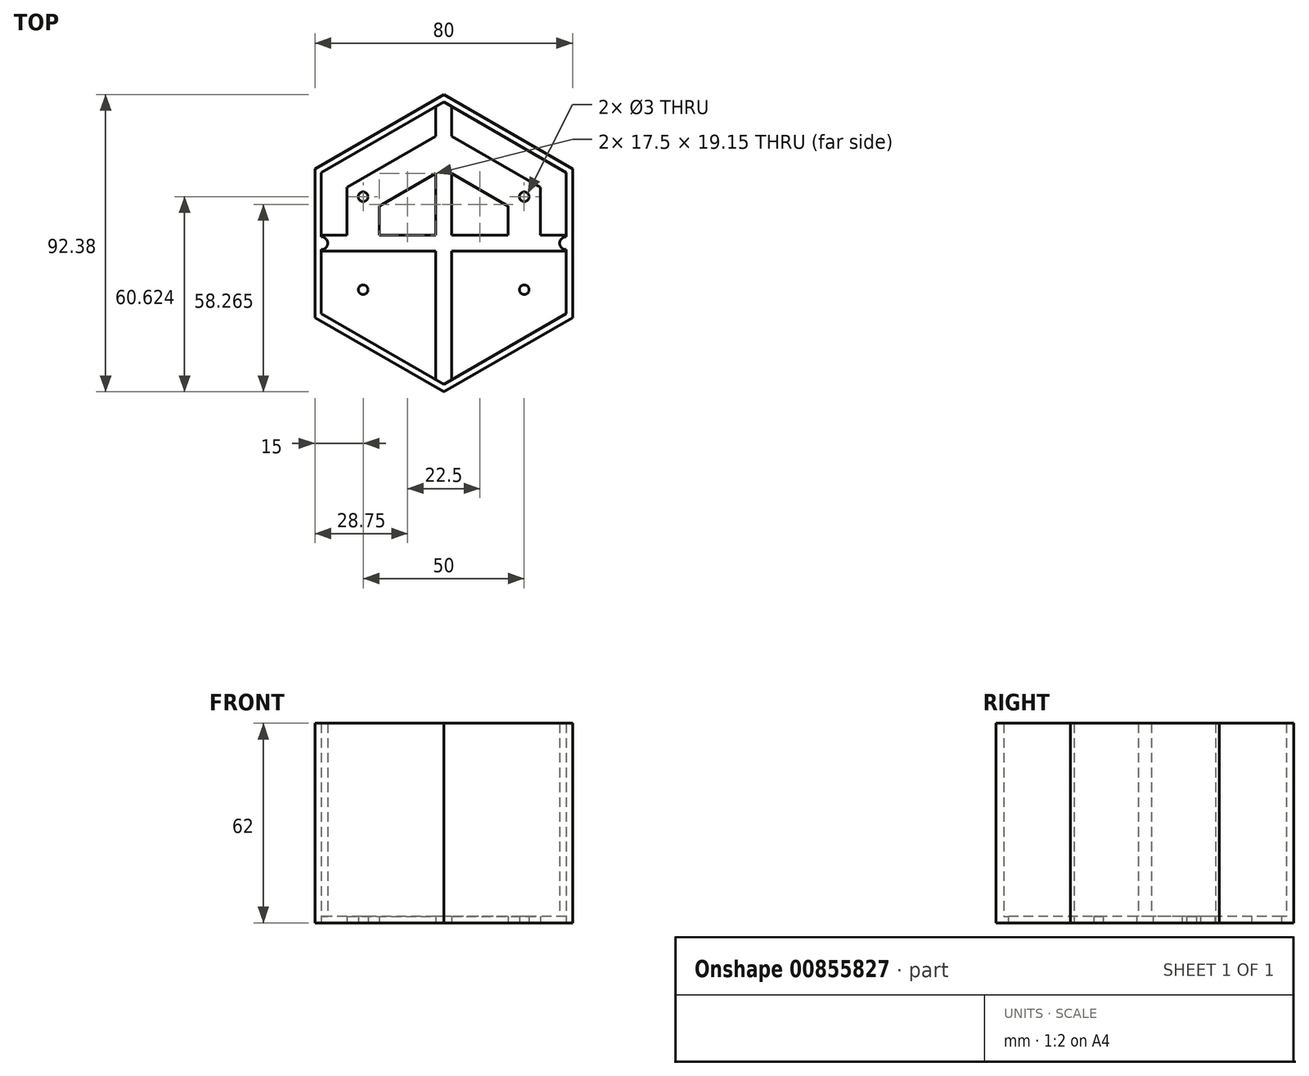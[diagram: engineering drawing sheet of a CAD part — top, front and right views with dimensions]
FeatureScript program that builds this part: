
annotation { "Feature Type Name" : "Feature", "Feature Type Description" : "" }
export const myFeature = defineFeature(function(context is Context, id is Id, definition is map)
    precondition{}
    {
        {
            var Q0;
            Q0=qCreatedBy(makeId("Top.planeOp"),FACE);
            var sketch = newSketch(context, id + "F0", { "sketchPlane" : qUnion([Q0])});
            skCircle(sketch, "E0.cCircle", {"center": v(0, 0) * mm, "radius": 40 * mm, "construction": true});
            skLineSegment(sketch, "E0.0", {"start": v(40, 23.1) * mm, "end": v(40, -23.1) * mm});
            skLineSegment(sketch, "E0.1", {"start": v(40, -23.1) * mm, "end": v(0, -46.19) * mm});
            skLineSegment(sketch, "E0.2", {"start": v(0, -46.19) * mm, "end": v(-40, -23.1) * mm});
            skLineSegment(sketch, "E0.3", {"start": v(-40, -23.1) * mm, "end": v(-40, 23.1) * mm});
            skLineSegment(sketch, "E0.4", {"start": v(-40, 23.1) * mm, "end": v(0, 46.19) * mm});
            skLineSegment(sketch, "E0.5", {"start": v(0, 46.19) * mm, "end": v(40, 23.1) * mm});
            skPoint(sketch, "E0.0.midPoint", {"position": v(40, 0) * mm});
            skCircle(sketch, "E1.cCircle", {"center": v(0, 0) * mm, "radius": 38 * mm, "construction": true});
            skLineSegment(sketch, "E1.0", {"start": v(38, 21.94) * mm, "end": v(38, -21.94) * mm});
            skLineSegment(sketch, "E1.1", {"start": v(38, -21.94) * mm, "end": v(0, -43.88) * mm});
            skLineSegment(sketch, "E1.2", {"start": v(0, -43.88) * mm, "end": v(-38, -21.94) * mm});
            skLineSegment(sketch, "E1.3", {"start": v(-38, -21.94) * mm, "end": v(-38, 21.94) * mm});
            skLineSegment(sketch, "E1.4", {"start": v(-38, 21.94) * mm, "end": v(0, 43.88) * mm});
            skLineSegment(sketch, "E1.5", {"start": v(0, 43.88) * mm, "end": v(38, 21.94) * mm});
            skPoint(sketch, "E1.0.midPoint", {"position": v(38, 0) * mm});
            skCircle(sketch, "E2.cCircle", {"center": v(0, 0) * mm, "radius": 30 * mm, "construction": true});
            skLineSegment(sketch, "E2.0", {"start": v(30, 17.32) * mm, "end": v(30, -17.32) * mm});
            skLineSegment(sketch, "E2.1", {"start": v(30, -17.32) * mm, "end": v(0, -34.64) * mm});
            skLineSegment(sketch, "E2.2", {"start": v(0, -34.64) * mm, "end": v(-30, -17.32) * mm});
            skLineSegment(sketch, "E2.3", {"start": v(-30, -17.32) * mm, "end": v(-30, 17.32) * mm});
            skLineSegment(sketch, "E2.4", {"start": v(-30, 17.32) * mm, "end": v(0, 34.64) * mm});
            skLineSegment(sketch, "E2.5", {"start": v(0, 34.64) * mm, "end": v(30, 17.32) * mm});
            skPoint(sketch, "E2.0.midPoint", {"position": v(30, 0) * mm});
            skCircle(sketch, "E3.cCircle", {"center": v(0, 0) * mm, "radius": 20 * mm, "construction": true});
            skLineSegment(sketch, "E3.0", {"start": v(20, 11.55) * mm, "end": v(20, -11.55) * mm});
            skLineSegment(sketch, "E3.1", {"start": v(20, -11.55) * mm, "end": v(0, -23.1) * mm});
            skLineSegment(sketch, "E3.2", {"start": v(0, -23.1) * mm, "end": v(-20, -11.55) * mm});
            skLineSegment(sketch, "E3.3", {"start": v(-20, -11.55) * mm, "end": v(-20, 11.55) * mm});
            skLineSegment(sketch, "E3.4", {"start": v(-20, 11.55) * mm, "end": v(0, 23.1) * mm});
            skLineSegment(sketch, "E3.5", {"start": v(0, 23.1) * mm, "end": v(20, 11.55) * mm});
            skPoint(sketch, "E3.0.midPoint", {"position": v(20, 0) * mm});
            skLineSegment(sketch, "E4.bottom", {"start": v(38, -2.5) * mm, "end": v(-38, -2.5) * mm});
            skLineSegment(sketch, "E4.top", {"start": v(38, 2.5) * mm, "end": v(-38, 2.5) * mm});
            skLineSegment(sketch, "E4.left", {"start": v(38, -2.5) * mm, "end": v(38, 2.5) * mm});
            skLineSegment(sketch, "E4.right", {"start": v(-38, -2.5) * mm, "end": v(-38, 2.5) * mm});
            skLineSegment(sketch, "E5.bottom", {"start": v(2.5, 44.74) * mm, "end": v(-2.5, 44.74) * mm});
            skLineSegment(sketch, "E5.top", {"start": v(2.5, -44.74) * mm, "end": v(-2.5, -44.74) * mm});
            skLineSegment(sketch, "E5.left", {"start": v(2.5, 44.74) * mm, "end": v(2.5, -44.74) * mm});
            skLineSegment(sketch, "E5.right", {"start": v(-2.5, 44.74) * mm, "end": v(-2.5, -44.74) * mm});
            skLineSegment(sketch, "E6", {"start": v(-30, 17.32) * mm, "end": v(-20, 11.55) * mm, "construction": true});
            skCircle(sketch, "E7", {"center": v(-25, 14.43) * mm, "radius": 1.5 * mm});
            skLineSegment(sketch, "E8", {"start": v(20, 11.55) * mm, "end": v(30, 17.32) * mm, "construction": true});
            skCircle(sketch, "E9", {"center": v(25, 14.43) * mm, "radius": 1.5 * mm});
            skLineSegment(sketch, "E10", {"start": v(-40, 0) * mm, "end": v(58.27, 0) * mm, "construction": true});
            skCircle(sketch, "E11.MirrorC", {"center": v(-25, -14.43) * mm, "radius": 1.5 * mm});
            skCircle(sketch, "E12.MirrorC", {"center": v(25, -14.43) * mm, "radius": 1.5 * mm});
            skArc(sketch, "E13", {"start": v(38, 2) * mm, "mid": v(36, 0) * mm, "end": v(38, -2) * mm});
            skArc(sketch, "E14", {"start": v(-38, -2) * mm, "mid": v(-36, 0) * mm, "end": v(-38, 2) * mm});
            skSolve(sketch);
        }
        {
            var Q0;
            {var subQ12=sQuery(id+"F0.wireOp",EDGE,"E5.bottom");var subQ18=sQuery(id+"F0.wireOp",EDGE,"E5.top");var subQ23=sQuery(id+"F0.wireOp",EDGE,"E0.3");var subQ40=sQuery(id+"F0.wireOp",EDGE,"E0.0");var subQ45=makeQuery(id+"F0.imprint","IMPRINT",EDGE,{"derivedFrom":subQ12});var subQ47=makeQuery(id+"F0.imprint","IMPRINT",EDGE,{"derivedFrom":subQ18});Q0=qUnion([makeQuery(id+"F0.imprint","IMPRINT",FACE,{"disambiguationData":[TD([[subQ47,1.0]])]}),makeQuery(id+"F0.imprint","IMPRINT",FACE,{"disambiguationData":[TD([[subQ45,-1.0]])]}),makeQuery(id+"F0.imprint","IMPRINT",FACE,{"disambiguationData":[TD([[subQ47,-1.0]])]}),makeQuery(id+"F0.imprint","IMPRINT",FACE,{"disambiguationData":[TD([[subQ45,1.0]])]}),makeQuery(id+"F0.imprint","IMPRINT",FACE,{"disambiguationData":[TD([[makeQuery(id+"F0.imprint","IMPRINT",EDGE,{"derivedFrom":subQ40}),-1.0]])]}),makeQuery(id+"F0.imprint","IMPRINT",FACE,{"disambiguationData":[TD([[makeQuery(id+"F0.imprint","IMPRINT",EDGE,{"derivedFrom":subQ23}),-1.0]])]})]);}
            var Q1;
            Q1=makeQuery(id+"F0.imprint","IMPRINT",FACE,{"disambiguationData":[TD([[makeQuery(id+"F0.imprint","IMPRINT",EDGE,{"derivedFrom":sQuery(id+"F0.wireOp",EDGE,"E7")}),-1.0]])]});
            var Q2;
            Q2=makeQuery(id+"F0.imprint","IMPRINT",FACE,{"disambiguationData":[TD([[makeQuery(id+"F0.imprint","IMPRINT",EDGE,{"derivedFrom":sQuery(id+"F0.wireOp",EDGE,"E9")}),-1.0]])]});
            var Q3;
            {var subQ7=sQuery(id+"F0.wireOp",EDGE,"E2.5");var subQ8=sQuery(id+"F0.wireOp",EDGE,"E2.4");var subQ9=makeQuery(id+"F0.imprint","INTERSECT",VERTEX,{"derivedFrom":[subQ8,subQ7]});Q3=makeQuery(id+"F0.imprint","IMPRINT",FACE,{"disambiguationData":[TD([[makeQuery(id+"F0.imprint","IMPRINT",EDGE,{"disambiguationData":[TD([[subQ9,1.0]])],"derivedFrom":subQ8}),-1.0]])]});}
            var Q4;
            {var subQ6=sQuery(id+"F0.wireOp",EDGE,"E1.4");var subQ9=sQuery(id+"F0.wireOp",EDGE,"E1.5");var subQ10=makeQuery(id+"F0.imprint","INTERSECT",VERTEX,{"derivedFrom":[subQ6,subQ9]});Q4=makeQuery(id+"F0.imprint","IMPRINT",FACE,{"disambiguationData":[TD([[makeQuery(id+"F0.imprint","IMPRINT",EDGE,{"disambiguationData":[TD([[subQ10,1.0]])],"derivedFrom":subQ6}),-1.0]])]});}
            var Q5;
            Q5=makeQuery(id+"F0.imprint","IMPRINT",FACE,{"disambiguationData":[TD([[makeQuery(id+"F0.imprint","IMPRINT",EDGE,{"derivedFrom":sQuery(id+"F0.wireOp",EDGE,"E11.MirrorC")}),1.0]])]});
            var Q6;
            {var subQ7=sQuery(id+"F0.wireOp",EDGE,"E2.2");var subQ8=sQuery(id+"F0.wireOp",EDGE,"E2.1");var subQ9=makeQuery(id+"F0.imprint","INTERSECT",VERTEX,{"derivedFrom":[subQ8,subQ7]});Q6=makeQuery(id+"F0.imprint","IMPRINT",FACE,{"disambiguationData":[TD([[makeQuery(id+"F0.imprint","IMPRINT",EDGE,{"disambiguationData":[TD([[subQ9,1.0]])],"derivedFrom":subQ8}),-1.0]])]});}
            var Q7;
            Q7=makeQuery(id+"F0.imprint","IMPRINT",FACE,{"disambiguationData":[TD([[makeQuery(id+"F0.imprint","IMPRINT",EDGE,{"derivedFrom":sQuery(id+"F0.wireOp",EDGE,"E12.MirrorC")}),1.0]])]});
            var Q8;
            {var subQ0=sQuery(id+"F0.wireOp",EDGE,"E4.bottom");var subQ1=sQuery(id+"F0.wireOp",EDGE,"E2.0");var subQ2=makeQuery(id+"F0.imprint","INTERSECT",VERTEX,{"derivedFrom":[subQ1,subQ0]});Q8=makeQuery(id+"F0.imprint","IMPRINT",FACE,{"disambiguationData":[TD([[makeQuery(id+"F0.imprint","IMPRINT",EDGE,{"disambiguationData":[TD([[subQ2,1.0]])],"derivedFrom":subQ1}),-1.0]])]});}
            var Q9;
            {var subQ5=sQuery(id+"F0.wireOp",EDGE,"E13");Q9=makeQuery(id+"F0.imprint","IMPRINT",FACE,{"disambiguationData":[TD([[makeQuery(id+"F0.imprint","IMPRINT",EDGE,{"derivedFrom":subQ5}),-1.0]])]});}
            var Q10;
            {var subQ0=sQuery(id+"F0.wireOp",EDGE,"E4.bottom");var subQ1=sQuery(id+"F0.wireOp",EDGE,"E3.0");var subQ2=makeQuery(id+"F0.imprint","INTERSECT",VERTEX,{"derivedFrom":[subQ1,subQ0]});Q10=makeQuery(id+"F0.imprint","IMPRINT",FACE,{"disambiguationData":[TD([[makeQuery(id+"F0.imprint","IMPRINT",EDGE,{"disambiguationData":[TD([[subQ2,1.0]])],"derivedFrom":subQ1}),-1.0]])]});}
            var Q11;
            {var subQ1=sQuery(id+"F0.wireOp",EDGE,"E3.5");var subQ7=sQuery(id+"F0.wireOp",EDGE,"E3.4");var subQ8=makeQuery(id+"F0.imprint","INTERSECT",VERTEX,{"derivedFrom":[subQ7,subQ1]});Q11=makeQuery(id+"F0.imprint","IMPRINT",FACE,{"disambiguationData":[TD([[makeQuery(id+"F0.imprint","IMPRINT",EDGE,{"disambiguationData":[TD([[subQ8,1.0]])],"derivedFrom":subQ7}),-1.0]])]});}
            var Q12;
            {var subQ0=sQuery(id+"F0.wireOp",EDGE,"E4.top");var subQ1=sQuery(id+"F0.wireOp",EDGE,"E3.3");var subQ2=makeQuery(id+"F0.imprint","INTERSECT",VERTEX,{"derivedFrom":[subQ1,subQ0]});Q12=makeQuery(id+"F0.imprint","IMPRINT",FACE,{"disambiguationData":[TD([[makeQuery(id+"F0.imprint","IMPRINT",EDGE,{"disambiguationData":[TD([[subQ2,1.0]])],"derivedFrom":subQ1}),-1.0]])]});}
            var Q13;
            {var subQ0=sQuery(id+"F0.wireOp",EDGE,"E4.top");var subQ1=sQuery(id+"F0.wireOp",EDGE,"E2.3");var subQ2=makeQuery(id+"F0.imprint","INTERSECT",VERTEX,{"derivedFrom":[subQ1,subQ0]});Q13=makeQuery(id+"F0.imprint","IMPRINT",FACE,{"disambiguationData":[TD([[makeQuery(id+"F0.imprint","IMPRINT",EDGE,{"disambiguationData":[TD([[subQ2,1.0]])],"derivedFrom":subQ1}),-1.0]])]});}
            var Q14;
            {var subQ5=sQuery(id+"F0.wireOp",EDGE,"E14");Q14=makeQuery(id+"F0.imprint","IMPRINT",FACE,{"disambiguationData":[TD([[makeQuery(id+"F0.imprint","IMPRINT",EDGE,{"derivedFrom":subQ5}),-1.0]])]});}
            var Q15;
            {var subQ5=sQuery(id+"F0.wireOp",EDGE,"E3.1");var subQ7=sQuery(id+"F0.wireOp",EDGE,"E3.2");var subQ8=makeQuery(id+"F0.imprint","INTERSECT",VERTEX,{"derivedFrom":[subQ5,subQ7]});Q15=makeQuery(id+"F0.imprint","IMPRINT",FACE,{"disambiguationData":[TD([[makeQuery(id+"F0.imprint","IMPRINT",EDGE,{"disambiguationData":[TD([[subQ8,1.0]])],"derivedFrom":subQ5}),-1.0]])]});}
            var Q16;
            {var subQ0=sQuery(id+"F0.wireOp",EDGE,"E5.right");var subQ1=sQuery(id+"F0.wireOp",EDGE,"E4.bottom");var subQ2=makeQuery(id+"F0.imprint","INTERSECT",VERTEX,{"derivedFrom":[subQ1,subQ0]});Q16=makeQuery(id+"F0.imprint","IMPRINT",FACE,{"disambiguationData":[TD([[makeQuery(id+"F0.imprint","IMPRINT",EDGE,{"disambiguationData":[TD([[subQ2,1.0]])],"derivedFrom":subQ1}),-1.0]])]});}
            var Q17;
            {var subQ7=sQuery(id+"F0.wireOp",EDGE,"E1.2");var subQ8=sQuery(id+"F0.wireOp",EDGE,"E1.1");var subQ9=makeQuery(id+"F0.imprint","INTERSECT",VERTEX,{"derivedFrom":[subQ8,subQ7]});Q17=makeQuery(id+"F0.imprint","IMPRINT",FACE,{"disambiguationData":[TD([[makeQuery(id+"F0.imprint","IMPRINT",EDGE,{"disambiguationData":[TD([[subQ9,1.0]])],"derivedFrom":subQ8}),-1.0]])]});}
            var Q18;
            {var subQ0=sQuery(id+"F0.wireOp",EDGE,"E14");Q18=makeQuery(id+"F0.imprint","IMPRINT",FACE,{"disambiguationData":[TD([[makeQuery(id+"F0.imprint","IMPRINT",EDGE,{"derivedFrom":subQ0}),1.0]])]});}
            var Q19;
            {var subQ0=sQuery(id+"F0.wireOp",EDGE,"E13");Q19=makeQuery(id+"F0.imprint","IMPRINT",FACE,{"disambiguationData":[TD([[makeQuery(id+"F0.imprint","IMPRINT",EDGE,{"derivedFrom":subQ0}),1.0]])]});}
            extrude(context, id + "F1", {"entities" : qUnion([Q0, Q1, Q2, Q3, Q4, Q5, Q6, Q7, Q8, Q9, Q10, Q11, Q12, Q13, Q14, Q15, Q16, Q17, Q18, Q19]), "depth" : 2 * mm, "offsetDistance" : 25 * mm});
        }
        {
            var Q0;
            Q0=makeQuery(id+"F1.opExtrude","CAP_FACE",FACE,{"disambiguationData":[OSD([sQuery(id+"F0.wireOp",EDGE,"E0.0"),sQuery(id+"F0.wireOp",EDGE,"E0.1"),sQuery(id+"F0.wireOp",EDGE,"E0.2"),sQuery(id+"F0.wireOp",EDGE,"E0.3"),sQuery(id+"F0.wireOp",EDGE,"E0.4"),sQuery(id+"F0.wireOp",EDGE,"E0.5"),sQuery(id+"F0.wireOp",EDGE,"E1.0"),sQuery(id+"F0.wireOp",EDGE,"E1.1"),sQuery(id+"F0.wireOp",EDGE,"E1.2"),sQuery(id+"F0.wireOp",EDGE,"E1.3"),sQuery(id+"F0.wireOp",EDGE,"E1.4"),sQuery(id+"F0.wireOp",EDGE,"E1.5"),sQuery(id+"F0.wireOp",EDGE,"E2.0"),sQuery(id+"F0.wireOp",EDGE,"E2.1"),sQuery(id+"F0.wireOp",EDGE,"E2.2"),sQuery(id+"F0.wireOp",EDGE,"E2.3"),sQuery(id+"F0.wireOp",EDGE,"E2.4"),sQuery(id+"F0.wireOp",EDGE,"E2.5"),sQuery(id+"F0.wireOp",EDGE,"E3.0"),sQuery(id+"F0.wireOp",EDGE,"E3.1"),sQuery(id+"F0.wireOp",EDGE,"E3.2"),sQuery(id+"F0.wireOp",EDGE,"E3.3"),sQuery(id+"F0.wireOp",EDGE,"E3.4"),sQuery(id+"F0.wireOp",EDGE,"E3.5"),sQuery(id+"F0.wireOp",EDGE,"E4.bottom"),sQuery(id+"F0.wireOp",EDGE,"E4.top"),sQuery(id+"F0.wireOp",EDGE,"E5.left"),sQuery(id+"F0.wireOp",EDGE,"E5.right"),sQuery(id+"F0.wireOp",EDGE,"E7"),sQuery(id+"F0.wireOp",EDGE,"E9"),sQuery(id+"F0.wireOp",EDGE,"E11.MirrorC"),sQuery(id+"F0.wireOp",EDGE,"E12.MirrorC")])],"isStart":false});
            var sketch = newSketch(context, id + "F2", { "sketchPlane" : qUnion([Q0])});
            skLineSegment(sketch, "E15.0", {"start": v(-38, -21.94) * mm, "end": v(-38, 21.94) * mm});
            skLineSegment(sketch, "E15.1", {"start": v(-40, -23.1) * mm, "end": v(-40, 23.1) * mm});
            skLineSegment(sketch, "E15.2", {"start": v(-40, 23.1) * mm, "end": v(0, 46.19) * mm});
            skLineSegment(sketch, "E15.3", {"start": v(-38, 21.94) * mm, "end": v(0, 43.88) * mm});
            skLineSegment(sketch, "E15.4", {"start": v(0, -43.88) * mm, "end": v(-38, -21.94) * mm});
            skLineSegment(sketch, "E15.5", {"start": v(0, -46.19) * mm, "end": v(-40, -23.1) * mm});
            skLineSegment(sketch, "E15.6", {"start": v(38, -21.94) * mm, "end": v(0, -43.88) * mm});
            skLineSegment(sketch, "E15.7", {"start": v(40, -23.1) * mm, "end": v(0, -46.19) * mm});
            skLineSegment(sketch, "E15.8", {"start": v(38, 21.94) * mm, "end": v(38, -21.94) * mm});
            skLineSegment(sketch, "E15.9", {"start": v(40, 23.1) * mm, "end": v(40, -23.1) * mm});
            skLineSegment(sketch, "E15.10", {"start": v(0, 46.19) * mm, "end": v(40, 23.1) * mm});
            skLineSegment(sketch, "E15.11", {"start": v(0, 43.88) * mm, "end": v(38, 21.94) * mm});
            skArc(sketch, "E16.0", {"start": v(-38, -2) * mm, "mid": v(-36, 0) * mm, "end": v(-38, 2) * mm});
            skArc(sketch, "E16.1", {"start": v(38, 2) * mm, "mid": v(36, 0) * mm, "end": v(38, -2) * mm});
            skSolve(sketch);
        }
        {
            var Q0;
            Q0 = qSketchRegion(id + "F2", true);
            var Q1;
            {var subQ0=sQuery(id+"F2.wireOp",EDGE,"E16.0");Q1=makeQuery(id+"F2.imprint","IMPRINT",FACE,{"disambiguationData":[TD([[makeQuery(id+"F2.imprint","IMPRINT",EDGE,{"derivedFrom":subQ0}),1.0]])]});}
            var Q2;
            {var subQ0=sQuery(id+"F2.wireOp",EDGE,"E16.1");Q2=makeQuery(id+"F2.imprint","IMPRINT",FACE,{"disambiguationData":[TD([[makeQuery(id+"F2.imprint","IMPRINT",EDGE,{"derivedFrom":subQ0}),1.0]])]});}
            extrude(context, id + "F3", {"entities" : qUnion([Q0, Q1, Q2]), "operationType" : NewBodyOperationType.ADD, "depth" : 60 * mm, "offsetDistance" : 25 * mm});
        }
    });
